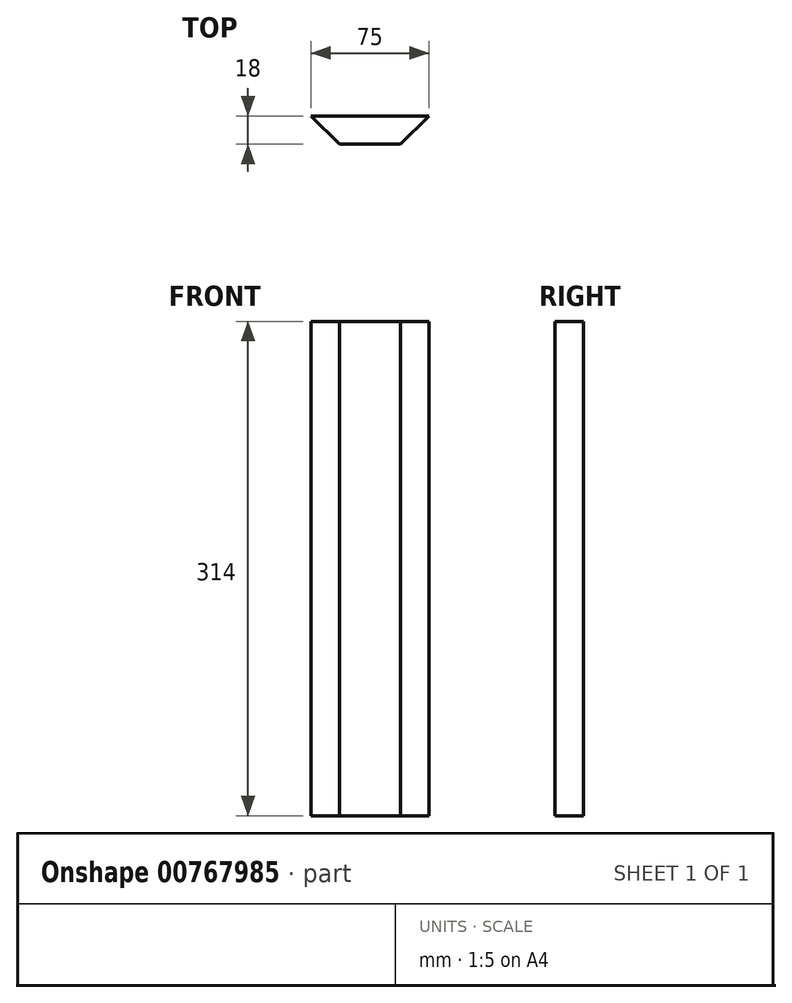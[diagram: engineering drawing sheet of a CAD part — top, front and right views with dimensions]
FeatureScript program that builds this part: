
annotation { "Feature Type Name" : "Feature", "Feature Type Description" : "" }
export const myFeature = defineFeature(function(context is Context, id is Id, definition is map)
    precondition{}
    {
        {
            var Q0;
            Q0=qCreatedBy(makeId("Front.planeOp"),FACE);
            var sketch = newSketch(context, id + "F0", { "sketchPlane" : qUnion([Q0])});
            skLineSegment(sketch, "E0.bottom", {"start": v(37.5, 157) * mm, "end": v(-37.5, 157) * mm});
            skLineSegment(sketch, "E0.top", {"start": v(37.5, -157) * mm, "end": v(-37.5, -157) * mm});
            skLineSegment(sketch, "E0.left", {"start": v(37.5, 157) * mm, "end": v(37.5, -157) * mm});
            skLineSegment(sketch, "E0.right", {"start": v(-37.5, 157) * mm, "end": v(-37.5, -157) * mm});
            skPoint(sketch, "E0.middle", {"position": v(0, 0) * mm});
            skSolve(sketch);
        }
        {
            var Q0;
            Q0 = qSketchRegion(id + "F0", true);
            extrude(context, id + "F1", {"entities" : qUnion([Q0]), "depth" : 18 * mm, "offsetDistance" : 25 * mm});
        }
        {
            var Q0;
            Q0=makeQuery(id+"F1.opExtrude","CAP_EDGE",EDGE,{"disambiguationData":[OSD([sQuery(id+"F0.wireOp",EDGE,"E0.left")])],"isStart":false});
            var Q1;
            Q1=makeQuery(id+"F1.opExtrude","CAP_EDGE",EDGE,{"disambiguationData":[OSD([sQuery(id+"F0.wireOp",EDGE,"E0.right")])],"isStart":false});
            chamfer(context, id + "F2", {"entities" : qUnion([Q0, Q1]), "width" : 18 * mm, "tangentPropagation" : true});
        }
    });
